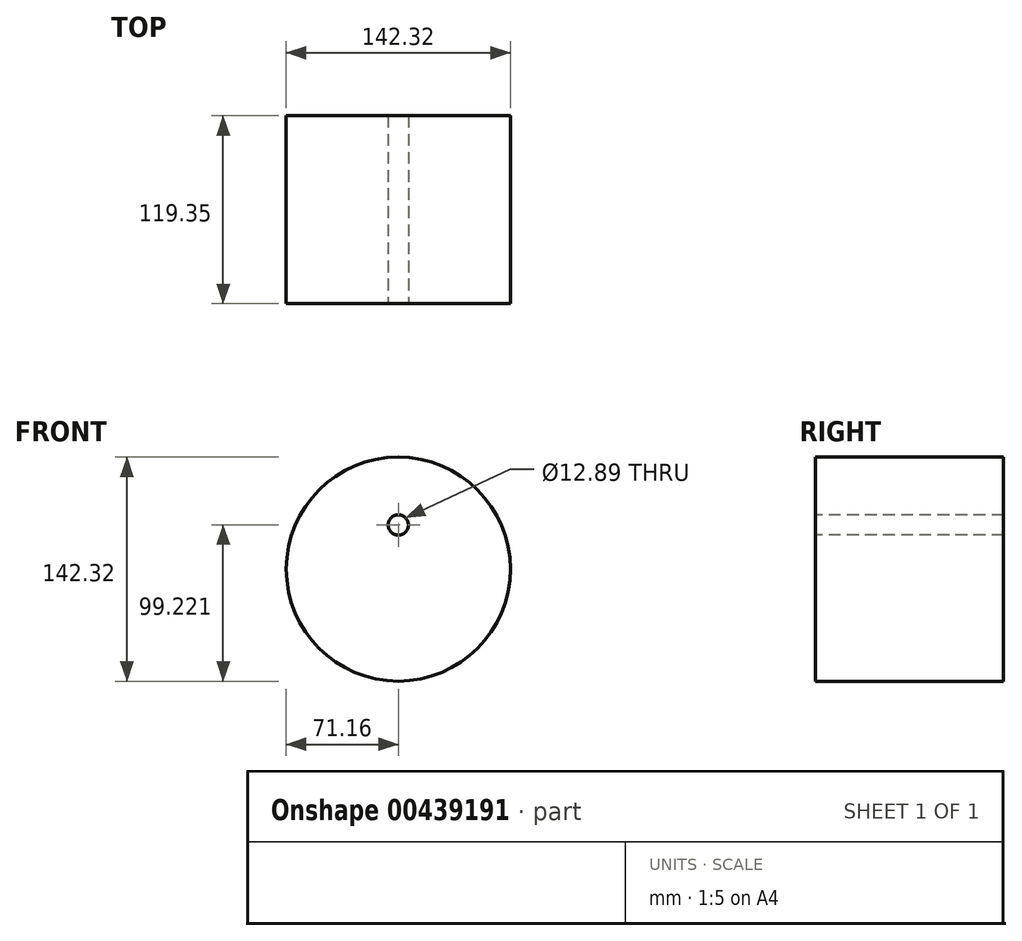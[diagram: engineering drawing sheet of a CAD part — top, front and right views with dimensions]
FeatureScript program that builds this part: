
annotation { "Feature Type Name" : "Feature", "Feature Type Description" : "" }
export const myFeature = defineFeature(function(context is Context, id is Id, definition is map)
    precondition{}
    {
        {
            var Q0;
            Q0=qCreatedBy(makeId("Front.planeOp"),FACE);
            var sketch = newSketch(context, id + "F0", { "sketchPlane" : qUnion([Q0])});
            skCircle(sketch, "E0", {"center": v(0, 0) * mm, "radius": 71.16 * mm});
            skSolve(sketch);
        }
        {
            var Q0;
            Q0=makeQuery(id+"F0.imprint","IMPRINT",FACE,{"disambiguationData":[TD([[makeQuery(id+"F0.imprint","IMPRINT",EDGE,{"derivedFrom":sQuery(id+"F0.wireOp",EDGE,"E0")}),1.0]])]});
            extrude(context, id + "F1", {"entities" : qUnion([Q0]), "oppositeDirection" : true, "depth" : 119.35 * mm});
        }
        {
            var Q0;
            Q0=qCreatedBy(makeId("Front.planeOp"),FACE);
            var sketch = newSketch(context, id + "F2", { "sketchPlane" : qUnion([Q0])});
            skCircle(sketch, "E1", {"center": v(0, 28.06) * mm, "radius": 6.45 * mm});
            skCircle(sketch, "E2", {"center": v(39.12, 0) * mm, "radius": 2.35 * mm});
            skSolve(sketch);
        }
        {
            var Q0;
            Q0=makeQuery(id+"F2.imprint","IMPRINT",FACE,{"disambiguationData":[TD([[makeQuery(id+"F2.imprint","IMPRINT",EDGE,{"derivedFrom":sQuery(id+"F2.wireOp",EDGE,"E1")}),1.0]])]});
            extrude(context, id + "F3", {"entities" : qUnion([Q0]), "operationType" : NewBodyOperationType.REMOVE, "oppositeDirection" : true, "depth" : 173.74 * mm});
        }
    });
